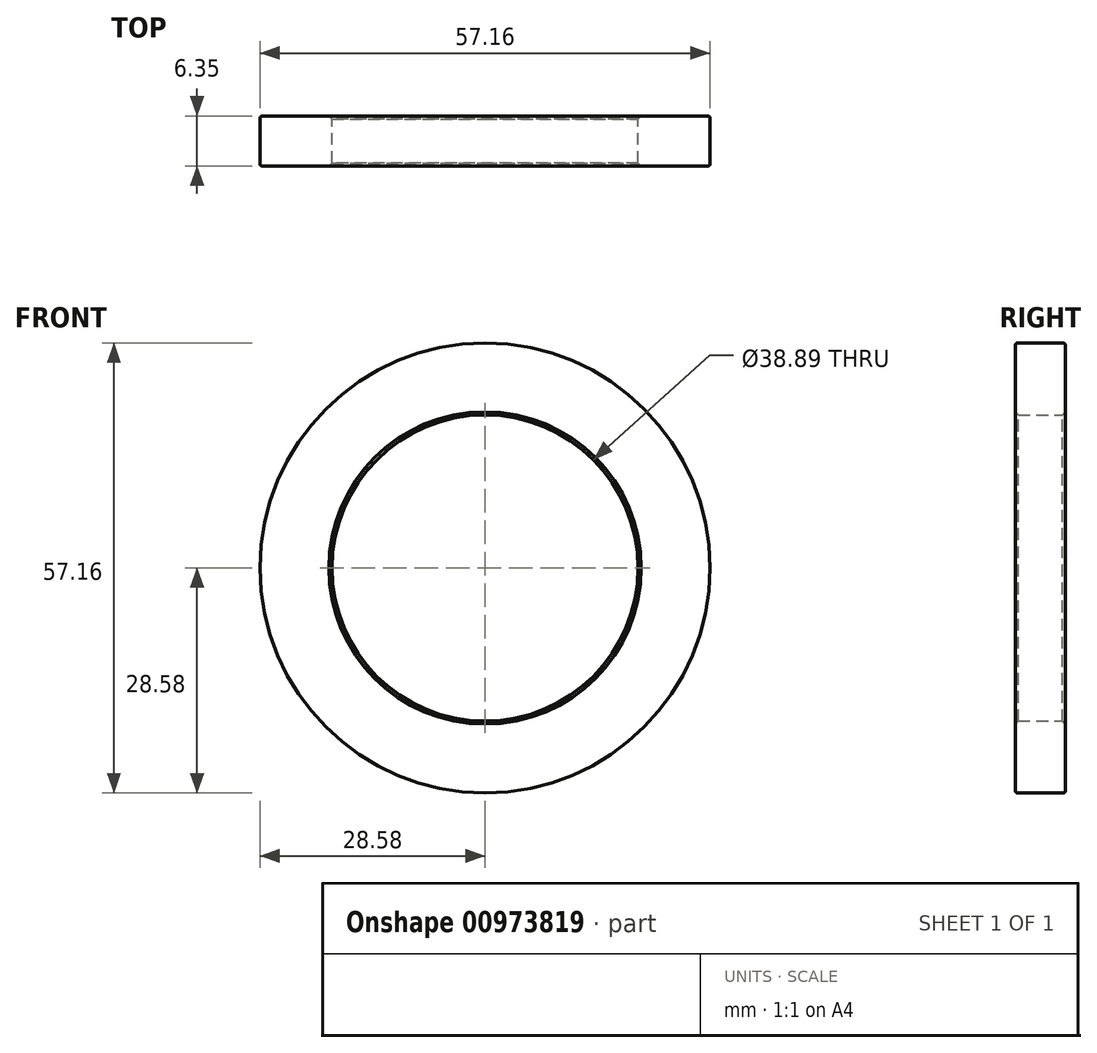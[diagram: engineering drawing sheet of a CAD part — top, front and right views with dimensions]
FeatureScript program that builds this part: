
annotation { "Feature Type Name" : "Feature", "Feature Type Description" : "" }
export const myFeature = defineFeature(function(context is Context, id is Id, definition is map)
    precondition{}
    {
        {
            var Q0;
            Q0=qCreatedBy(makeId("Front.planeOp"),FACE);
            var sketch = newSketch(context, id + "F0", { "sketchPlane" : qUnion([Q0])});
            skCircle(sketch, "E0", {"center": v(0, 0) * mm, "radius": 19.44 * mm});
            skLineSegment(sketch, "E1", {"start": v(28.58, 0) * mm, "end": v(28.58, 32) * mm, "construction": true});
            skCircle(sketch, "E2", {"center": v(0, 0) * mm, "radius": 28.58 * mm});
            skSolve(sketch);
        }
        {
            var Q0;
            Q0=makeQuery(id+"F0.imprint","IMPRINT",FACE,{"disambiguationData":[TD([[makeQuery(id+"F0.imprint","IMPRINT",EDGE,{"derivedFrom":sQuery(id+"F0.wireOp",EDGE,"E0")}),-1.0]])]});
            extrude(context, id + "F1", {"entities" : qUnion([Q0]), "depth" : 6.35 * mm, "offsetDistance" : 25.4 * mm});
        }
        {
            var Q0;
            Q0=makeQuery(id+"F1.opExtrude","CAP_EDGE",EDGE,{"disambiguationData":[OSD([sQuery(id+"F0.wireOp",EDGE,"E0")])],"isStart":false});
            var Q1;
            Q1=makeQuery(id+"F1.opExtrude","CAP_EDGE",EDGE,{"disambiguationData":[OSD([sQuery(id+"F0.wireOp",EDGE,"E0")])],"isStart":true});
            chamfer(context, id + "F2", {"entities" : qUnion([Q0, Q1]), "width" : 0.38 * mm, "tangentPropagation" : true});
        }
        {
            var Q0;
            Q0=makeQuery(id+"F1.opExtrude","CAP_EDGE",EDGE,{"disambiguationData":[OSD([sQuery(id+"F0.wireOp",EDGE,"E2")])],"isStart":true});
            var Q1;
            Q1=makeQuery(id+"F1.opExtrude","CAP_EDGE",EDGE,{"disambiguationData":[OSD([sQuery(id+"F0.wireOp",EDGE,"E2")])],"isStart":false});
            fillet(context, id + "F3", {"entities" : qUnion([Q0, Q1]), "radius" : 0.25 * mm, "tangentPropagation" : true, "allowEdgeOverflow" : false});
        }
    });
